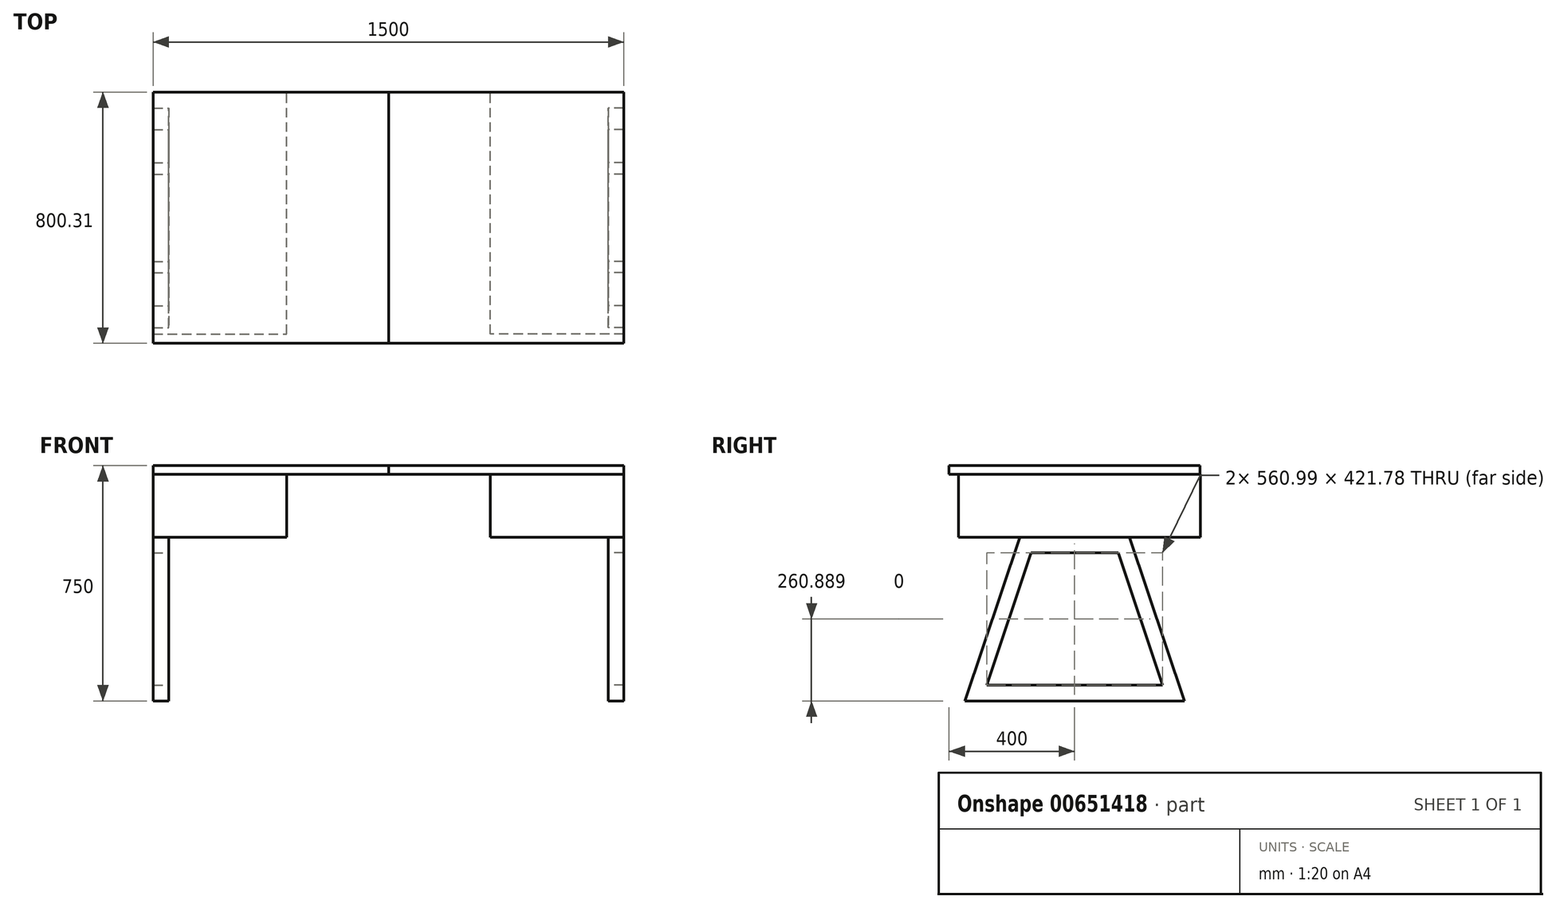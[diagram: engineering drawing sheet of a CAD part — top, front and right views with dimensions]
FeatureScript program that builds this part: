
annotation { "Feature Type Name" : "Feature", "Feature Type Description" : "" }
export const myFeature = defineFeature(function(context is Context, id is Id, definition is map)
    precondition{}
    {
        {
            assignVariable(context, id + "F0", {"name" : "b_desk", "anyValue" : 1500});
        }
        {
            var Q0;
            Q0=qCreatedBy(makeId("Right.planeOp"),FACE);
            var sketch = newSketch(context, id + "F1", { "sketchPlane" : qUnion([Q0])});
            skLineSegment(sketch, "E0.bottom", {"start": v(-400, 750) * mm, "end": v(400, 750) * mm});
            skLineSegment(sketch, "E0.top", {"start": v(-400, 722) * mm, "end": v(400, 722) * mm});
            skLineSegment(sketch, "E0.left", {"start": v(-400, 750) * mm, "end": v(-400, 722) * mm});
            skLineSegment(sketch, "E0.right", {"start": v(400, 750) * mm, "end": v(400, 722) * mm});
            skLineSegment(sketch, "E1", {"start": v(0, 750) * mm, "end": v(0, 0) * mm, "construction": true});
            skLineSegment(sketch, "E2.bottom", {"start": v(-175, 521.78) * mm, "end": v(175, 521.78) * mm});
            skLineSegment(sketch, "E3", {"start": v(-175, 521.78) * mm, "end": v(-350, 0) * mm});
            skLineSegment(sketch, "E4", {"start": v(-350, 0) * mm, "end": v(350, 0) * mm});
            skLineSegment(sketch, "E5", {"start": v(350, 0) * mm, "end": v(175, 521.78) * mm});
            skLineSegment(sketch, "E6", {"start": v(-139.03, 471.78) * mm, "end": v(139.03, 471.78) * mm});
            skLineSegment(sketch, "E7", {"start": v(139.03, 471.78) * mm, "end": v(280.5, 50) * mm});
            skLineSegment(sketch, "E8", {"start": v(280.5, 50) * mm, "end": v(-280.5, 50) * mm});
            skLineSegment(sketch, "E9", {"start": v(-280.5, 50) * mm, "end": v(-139.03, 471.78) * mm});
            skLineSegment(sketch, "E10", {"start": v(0, 521.78) * mm, "end": v(0, 471.78) * mm, "construction": true});
            skLineSegment(sketch, "E11", {"start": v(0, 471.78) * mm, "end": v(0, 0) * mm, "construction": true});
            skLineSegment(sketch, "E12", {"start": v(0, 0) * mm, "end": v(0, 50) * mm, "construction": true});
            skLineSegment(sketch, "E13.bottom", {"start": v(-370, 722) * mm, "end": v(400.3, 722) * mm});
            skLineSegment(sketch, "E13.top", {"start": v(-370, 522) * mm, "end": v(400.3, 522) * mm});
            skLineSegment(sketch, "E13.left", {"start": v(-370, 722) * mm, "end": v(-370, 522) * mm});
            skLineSegment(sketch, "E13.right", {"start": v(400.3, 722) * mm, "end": v(400.3, 522) * mm});
            skSolve(sketch);
        }
        {
            var Q0;
            Q0=makeQuery(id+"F1.imprint","IMPRINT",FACE,{"disambiguationData":[TD([[makeQuery(id+"F1.imprint","IMPRINT",EDGE,{"derivedFrom":sQuery(id+"F1.wireOp",EDGE,"E0.bottom")}),-1.0]])]});
            extrude(context, id + "F2", {"entities" : qUnion([Q0]), "depth" : (getVariable(context, 'b_desk') / 2) * mm, "offsetDistance" : 25 * mm});
        }
        {
            var Q0;
            Q0=makeQuery(id+"F1.imprint","IMPRINT",FACE,{"disambiguationData":[TD([[makeQuery(id+"F1.imprint","IMPRINT",EDGE,{"derivedFrom":sQuery(id+"F1.wireOp",EDGE,"E2.bottom")}),-1.0]])]});
            extrude(context, id + "F3", {"entities" : qUnion([Q0]), "depth" : (getVariable(context, 'b_desk') / 2) * mm, "offsetDistance" : 25 * mm, "hasSecondDirection" : true, "secondDirectionOppositeDirection" : false, "secondDirectionDepth" : (getVariable(context, 'b_desk') / 2 - 50) * mm});
        }
        {
            var Q0;
            Q0=makeQuery(id+"F2.opExtrude","SWEPT_BODY",BODY,{"disambiguationData":[OSD([sQuery(id+"F1.wireOp",EDGE,"E0.bottom"),sQuery(id+"F1.wireOp",EDGE,"E0.top"),sQuery(id+"F1.wireOp",EDGE,"E0.left"),sQuery(id+"F1.wireOp",EDGE,"E0.right"),sQuery(id+"F1.wireOp",EDGE,"E2.bottom")])]});
            var Q1;
            Q1=makeQuery(id+"F3.opExtrude","SWEPT_BODY",BODY,{"disambiguationData":[OSD([sQuery(id+"F1.wireOp",EDGE,"E2.bottom"),sQuery(id+"F1.wireOp",EDGE,"E3"),sQuery(id+"F1.wireOp",EDGE,"E4"),sQuery(id+"F1.wireOp",EDGE,"E5"),sQuery(id+"F1.wireOp",EDGE,"E6"),sQuery(id+"F1.wireOp",EDGE,"E7"),sQuery(id+"F1.wireOp",EDGE,"E8"),sQuery(id+"F1.wireOp",EDGE,"E9")])]});
            var Q2;
            Q2=qCreatedBy(makeId("Right.planeOp"),FACE);
            mirror(context, id + "F4", {"entities" : qUnion([Q0, Q1]), "mirrorPlane" : qUnion([Q2])});
        }
        {
            var Q0;
            Q0=makeQuery(id+"F1.imprint","IMPRINT",FACE,{"disambiguationData":[TD([[makeQuery(id+"F1.imprint","IMPRINT",EDGE,{"derivedFrom":sQuery(id+"F1.wireOp",EDGE,"E13.bottom")}),-1.0]])]});
            extrude(context, id + "F5", {"entities" : qUnion([Q0]), "depth" : (getVariable(context, 'b_desk') / 2) * mm, "offsetDistance" : 25 * mm, "hasSecondDirection" : true, "secondDirectionOppositeDirection" : false, "secondDirectionDepth" : (650 / 2) * mm});
        }
        {
            var Q0;
            Q0=makeQuery(id+"F5.opExtrude","SWEPT_BODY",BODY,{"disambiguationData":[OSD([sQuery(id+"F1.wireOp",EDGE,"E13.bottom"),sQuery(id+"F1.wireOp",EDGE,"E13.top"),sQuery(id+"F1.wireOp",EDGE,"E13.left"),sQuery(id+"F1.wireOp",EDGE,"E13.right")])]});
            var Q1;
            Q1=qCreatedBy(makeId("Right.planeOp"),FACE);
            mirror(context, id + "F6", {"entities" : qUnion([Q0]), "mirrorPlane" : qUnion([Q1])});
        }
    });
